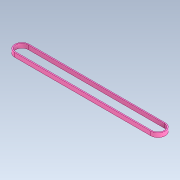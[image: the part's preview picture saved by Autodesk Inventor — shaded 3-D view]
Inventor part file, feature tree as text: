
AUTODESK INVENTOR PART (.ipt)
format: ipt  version: 2022 (Build 260153000, 153)  size: 88,576 bytes
history: native  units: mm
features: extrude x1, sketch x1
ambient origin geometry x8: Origin, YZ Plane, XZ Plane, XY Plane, X Axis, Y Axis, Z Axis, Center Point
bodies: Solid1 (feature_tree)
feature tree (2):
  extrude  "Extrusion1"  Depth=33.03mm
  sketch  "Sketch1"  dims[d0=3.0mm d1=33.03mm d2=3.0mm d3=3.5mm d4=1.0mm d5=0.0mm]
